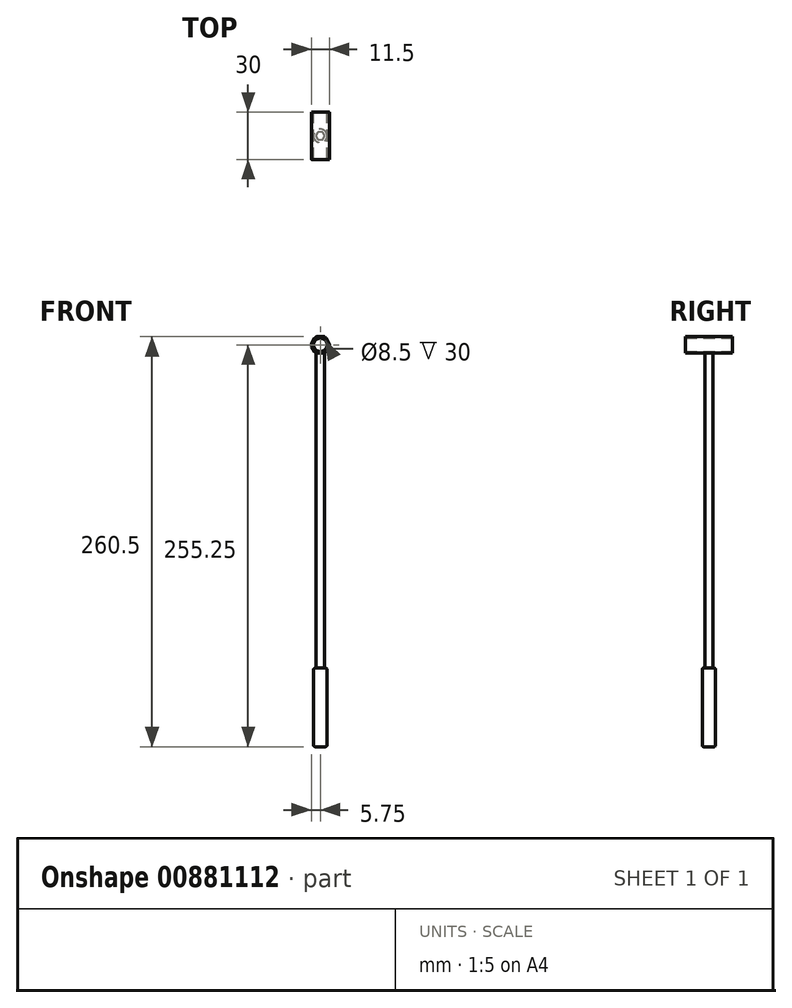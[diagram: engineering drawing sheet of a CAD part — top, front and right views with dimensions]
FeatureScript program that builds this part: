
annotation { "Feature Type Name" : "Feature", "Feature Type Description" : "" }
export const myFeature = defineFeature(function(context is Context, id is Id, definition is map)
    precondition{}
    {
        {
            var Q0;
            Q0=qCreatedBy(makeId("Front.planeOp"),FACE);
            var sketch = newSketch(context, id + "F0", { "sketchPlane" : qUnion([Q0])});
            skCircle(sketch, "E0", {"center": v(0, 0) * mm, "radius": 4.25 * mm});
            skLineSegment(sketch, "E1.0", {"start": v(-3.03, 5.25) * mm, "end": v(3.03, 5.25) * mm});
            skLineSegment(sketch, "E1.1", {"start": v(3.03, 5.25) * mm, "end": v(6.06, 0) * mm});
            skLineSegment(sketch, "E1.2", {"start": v(6.06, 0) * mm, "end": v(3.03, -5.25) * mm});
            skLineSegment(sketch, "E1.3", {"start": v(3.03, -5.25) * mm, "end": v(-3.03, -5.25) * mm});
            skLineSegment(sketch, "E1.4", {"start": v(-3.03, -5.25) * mm, "end": v(-6.06, 0) * mm});
            skLineSegment(sketch, "E1.5", {"start": v(-6.06, 0) * mm, "end": v(-3.03, 5.25) * mm});
            skPoint(sketch, "E1.0.midPoint", {"position": v(0, 5.25) * mm});
            skSolve(sketch);
        }
        {
            var Q0;
            Q0=makeQuery(id+"F0.imprint","IMPRINT",FACE,{"disambiguationData":[TD([[makeQuery(id+"F0.imprint","IMPRINT",EDGE,{"derivedFrom":sQuery(id+"F0.wireOp",EDGE,"E0")}),-1.0]])]});
            extrude(context, id + "F1", {"entities" : qUnion([Q0]), "depth" : 30 * mm, "offsetDistance" : 25 * mm});
        }
        {
            var Q0;
            Q0=makeQuery(id+"F1.opExtrude","SWEPT_FACE",FACE,{"disambiguationData":[OSD([sQuery(id+"F0.wireOp",EDGE,"E1.3")])]});
            var sketch = newSketch(context, id + "F2", { "sketchPlane" : qUnion([Q0])});
            skLineSegment(sketch, "E2", {"start": v(0, 0) * mm, "end": v(0, 15) * mm});
            skPoint(sketch, "E2.endSnap0", {"position": v(3.03, 15) * mm});
            skCircle(sketch, "E3.cCircle", {"center": v(0, 15) * mm, "radius": 2.5 * mm, "construction": true});
            skLineSegment(sketch, "E3.0", {"start": v(-1.44, 17.5) * mm, "end": v(1.44, 17.5) * mm});
            skLineSegment(sketch, "E3.1", {"start": v(1.44, 17.5) * mm, "end": v(2.89, 15) * mm});
            skLineSegment(sketch, "E3.2", {"start": v(2.89, 15) * mm, "end": v(1.44, 12.5) * mm});
            skLineSegment(sketch, "E3.3", {"start": v(1.44, 12.5) * mm, "end": v(-1.44, 12.5) * mm});
            skLineSegment(sketch, "E3.4", {"start": v(-1.44, 12.5) * mm, "end": v(-2.89, 15) * mm});
            skLineSegment(sketch, "E3.5", {"start": v(-2.89, 15) * mm, "end": v(-1.44, 17.5) * mm});
            skPoint(sketch, "E3.0.midPoint", {"position": v(0, 17.5) * mm});
            skSolve(sketch);
        }
        {
            var Q0;
            Q0=makeQuery(id+"F2.imprint","IMPRINT",FACE,{"disambiguationData":[TD([[makeQuery(id+"F2.imprint","IMPRINT",EDGE,{"derivedFrom":sQuery(id+"F2.wireOp",EDGE,"E3.0")}),-1.0]])]});
            extrude(context, id + "F3", {"entities" : qUnion([Q0]), "operationType" : NewBodyOperationType.ADD, "depth" : 200 * mm, "offsetDistance" : 25 * mm});
        }
        {
            var Q0;
            Q0=makeQuery(id+"F3.opExtrude","CAP_FACE",FACE,{"disambiguationData":[OSD([sQuery(id+"F2.wireOp",EDGE,"E3.0"),sQuery(id+"F2.wireOp",EDGE,"E3.1"),sQuery(id+"F2.wireOp",EDGE,"E3.2"),sQuery(id+"F2.wireOp",EDGE,"E3.3"),sQuery(id+"F2.wireOp",EDGE,"E3.4"),sQuery(id+"F2.wireOp",EDGE,"E3.5")])],"isStart":false});
            var sketch = newSketch(context, id + "F4", { "sketchPlane" : qUnion([Q0])});
            skCircle(sketch, "E4", {"center": v(0, 15) * mm, "radius": 4.25 * mm});
            skPoint(sketch, "E5.orphan", {"position": v(0, 17.5) * mm});
            skPoint(sketch, "E6.start.orphan", {"position": v(0, 12.5) * mm});
            skSolve(sketch);
        }
        {
            var Q0;
            Q0=makeQuery(id+"F4.imprint","IMPRINT",FACE,{"disambiguationData":[TD([[makeQuery(id+"F4.imprint","IMPRINT",EDGE,{"derivedFrom":sQuery(id+"F4.wireOp",EDGE,"E4")}),1.0]])]});
            var Q1;
            Q1=makeQuery(id+"F4.imprint","IMPRINT",FACE,{"disambiguationData":[TD([[makeQuery(id+"F4.imprint","IMPRINT",EDGE,{"derivedFrom":makeQuery(id+"F3.opExtrude","CAP_EDGE",EDGE,{"disambiguationData":[OSD([sQuery(id+"F2.wireOp",EDGE,"E3.0")])],"isStart":false})}),-1.0]])]});
            extrude(context, id + "F5", {"entities" : qUnion([Q0, Q1]), "operationType" : NewBodyOperationType.ADD, "depth" : 50 * mm, "offsetDistance" : 25 * mm});
        }
        {
            var Q0;
            Q0=makeQuery(id+"F1.opExtrude","SWEPT_EDGE",EDGE,{"disambiguationData":[OSD([sQuery(id+"F0.wireOp",EDGE,"E1.2"),sQuery(id+"F0.wireOp",EDGE,"E1.3")])]});
            var Q1;
            Q1=makeQuery(id+"F1.opExtrude","SWEPT_EDGE",EDGE,{"disambiguationData":[OSD([sQuery(id+"F0.wireOp",EDGE,"E1.3"),sQuery(id+"F0.wireOp",EDGE,"E1.4")])]});
            var Q2;
            Q2=makeQuery(id+"F1.opExtrude","SWEPT_EDGE",EDGE,{"disambiguationData":[OSD([sQuery(id+"F0.wireOp",EDGE,"E1.1"),sQuery(id+"F0.wireOp",EDGE,"E1.2")])]});
            var Q3;
            Q3=makeQuery(id+"F1.opExtrude","SWEPT_EDGE",EDGE,{"disambiguationData":[OSD([sQuery(id+"F0.wireOp",EDGE,"E1.0"),sQuery(id+"F0.wireOp",EDGE,"E1.1")])]});
            var Q4;
            Q4=makeQuery(id+"F1.opExtrude","SWEPT_EDGE",EDGE,{"disambiguationData":[OSD([sQuery(id+"F0.wireOp",EDGE,"E1.0"),sQuery(id+"F0.wireOp",EDGE,"E1.5")])]});
            var Q5;
            Q5=makeQuery(id+"F1.opExtrude","SWEPT_EDGE",EDGE,{"disambiguationData":[OSD([sQuery(id+"F0.wireOp",EDGE,"E1.4"),sQuery(id+"F0.wireOp",EDGE,"E1.5")])]});
            fillet(context, id + "F6", {"entities" : qUnion([Q0, Q1, Q2, Q3, Q4, Q5]), "radius" : 2 * mm, "tangentPropagation" : true, "allowEdgeOverflow" : false});
        }
        {
            var Q0;
            Q0=makeQuery(id+"F3.opExtrude","SWEPT_EDGE",EDGE,{"disambiguationData":[OSD([sQuery(id+"F2.wireOp",EDGE,"E3.0"),sQuery(id+"F2.wireOp",EDGE,"E3.5")])]});
            var Q1;
            Q1=makeQuery(id+"F3.opExtrude","SWEPT_EDGE",EDGE,{"disambiguationData":[OSD([sQuery(id+"F2.wireOp",EDGE,"E3.0"),sQuery(id+"F2.wireOp",EDGE,"E3.1")])]});
            var Q2;
            Q2=makeQuery(id+"F3.opExtrude","SWEPT_EDGE",EDGE,{"disambiguationData":[OSD([sQuery(id+"F2.wireOp",EDGE,"E3.4"),sQuery(id+"F2.wireOp",EDGE,"E3.5")])]});
            var Q3;
            Q3=makeQuery(id+"F3.opExtrude","SWEPT_EDGE",EDGE,{"disambiguationData":[OSD([sQuery(id+"F2.wireOp",EDGE,"E3.3"),sQuery(id+"F2.wireOp",EDGE,"E3.4")])]});
            var Q4;
            Q4=makeQuery(id+"F3.opExtrude","SWEPT_EDGE",EDGE,{"disambiguationData":[OSD([sQuery(id+"F2.wireOp",EDGE,"E3.1"),sQuery(id+"F2.wireOp",EDGE,"E3.2")])]});
            var Q5;
            Q5=makeQuery(id+"F3.opExtrude","SWEPT_EDGE",EDGE,{"disambiguationData":[OSD([sQuery(id+"F2.wireOp",EDGE,"E3.2"),sQuery(id+"F2.wireOp",EDGE,"E3.3")])]});
            fillet(context, id + "F7", {"entities" : qUnion([Q0, Q1, Q2, Q3, Q4, Q5]), "radius" : 1 * mm, "tangentPropagation" : true, "allowEdgeOverflow" : false});
        }
        {
            var Q0;
            Q0=makeQuery(id+"F5.opExtrude","CAP_EDGE",EDGE,{"disambiguationData":[OSD([sQuery(id+"F4.wireOp",EDGE,"E4")])],"isStart":false});
            var Q1;
            Q1=makeQuery(id+"F5.opExtrude","CAP_EDGE",EDGE,{"disambiguationData":[OSD([sQuery(id+"F4.wireOp",EDGE,"E4")])],"isStart":true});
            fillet(context, id + "F8", {"entities" : qUnion([Q0, Q1]), "radius" : 1 * mm, "tangentPropagation" : true, "allowEdgeOverflow" : false});
        }
    });
